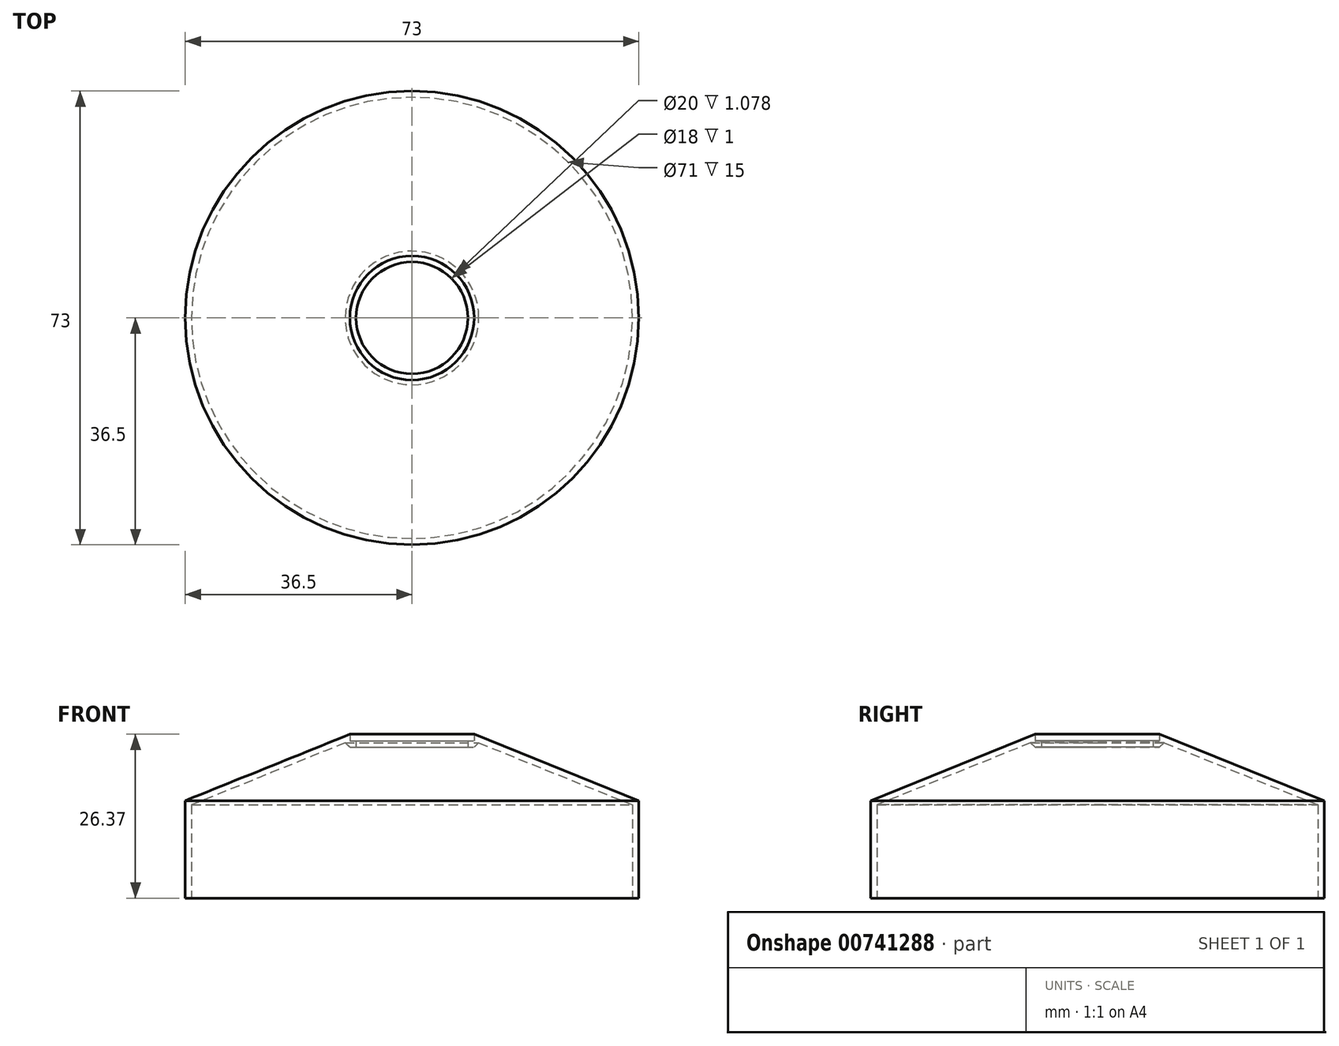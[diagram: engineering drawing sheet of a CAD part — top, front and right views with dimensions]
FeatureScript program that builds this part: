
annotation { "Feature Type Name" : "Feature", "Feature Type Description" : "" }
export const myFeature = defineFeature(function(context is Context, id is Id, definition is map)
    precondition{}
    {
        {
            var Q0;
            Q0=qCreatedBy(makeId("Front.planeOp"),FACE);
            var sketch = newSketch(context, id + "F0", { "sketchPlane" : qUnion([Q0])});
            skLineSegment(sketch, "E0", {"start": v(35.5, 25) * mm, "end": v(35.5, 40) * mm});
            skLineSegment(sketch, "E1", {"start": v(35.5, 40) * mm, "end": v(10, 50.3) * mm});
            skLineSegment(sketch, "E2", {"start": v(0, 0) * mm, "end": v(0, 97.12) * mm});
            skLineSegment(sketch, "E3", {"start": v(35.5, 25) * mm, "end": v(36.5, 25) * mm});
            skLineSegment(sketch, "E4", {"start": v(36.5, 25) * mm, "end": v(36.5, 40.67) * mm});
            skLineSegment(sketch, "E5", {"start": v(36.5, 40.67) * mm, "end": v(10, 51.37) * mm});
            skLineSegment(sketch, "E6", {"start": v(10, 51.37) * mm, "end": v(10, 50.3) * mm});
            skLineSegment(sketch, "E7", {"start": v(10, 50.3) * mm, "end": v(9, 50.3) * mm});
            skLineSegment(sketch, "E8", {"start": v(9, 50.3) * mm, "end": v(9, 49.3) * mm});
            skLineSegment(sketch, "E9", {"start": v(9, 49.3) * mm, "end": v(10, 49.3) * mm});
            skLineSegment(sketch, "E10", {"start": v(10, 49.3) * mm, "end": v(10, 50.3) * mm});
            skLineSegment(sketch, "E11", {"start": v(10, 49.3) * mm, "end": v(10.75, 50) * mm});
            skSolve(sketch);
        }
        {
            var Q0;
            Q0 = qSketchRegion(id + "F0", true);
            var Q1;
            Q1=sQuery(id+"F0.wireOp",EDGE,"E1");
            var Q2;
            Q2=sQuery(id+"F0.wireOp",EDGE,"E0");
            var Q3;
            Q3=sQuery(id+"F0.wireOp",EDGE,"9m7WS30J-CQfu-ofj0-xoV4-6mp1uTeQsaJ3");
            var Q4;
            Q4=sQuery(id+"F0.wireOp",EDGE,"E2");
            revolve(context, id + "F1", {"surfaceOperationType" : NewSurfaceOperationType.NEW, "entities" : qUnion([Q0]), "surfaceEntities" : qUnion([Q1, Q2, Q3]), "axis" : qUnion([Q4]), "revolveType" : RevolveType.FULL});
        }
    });
